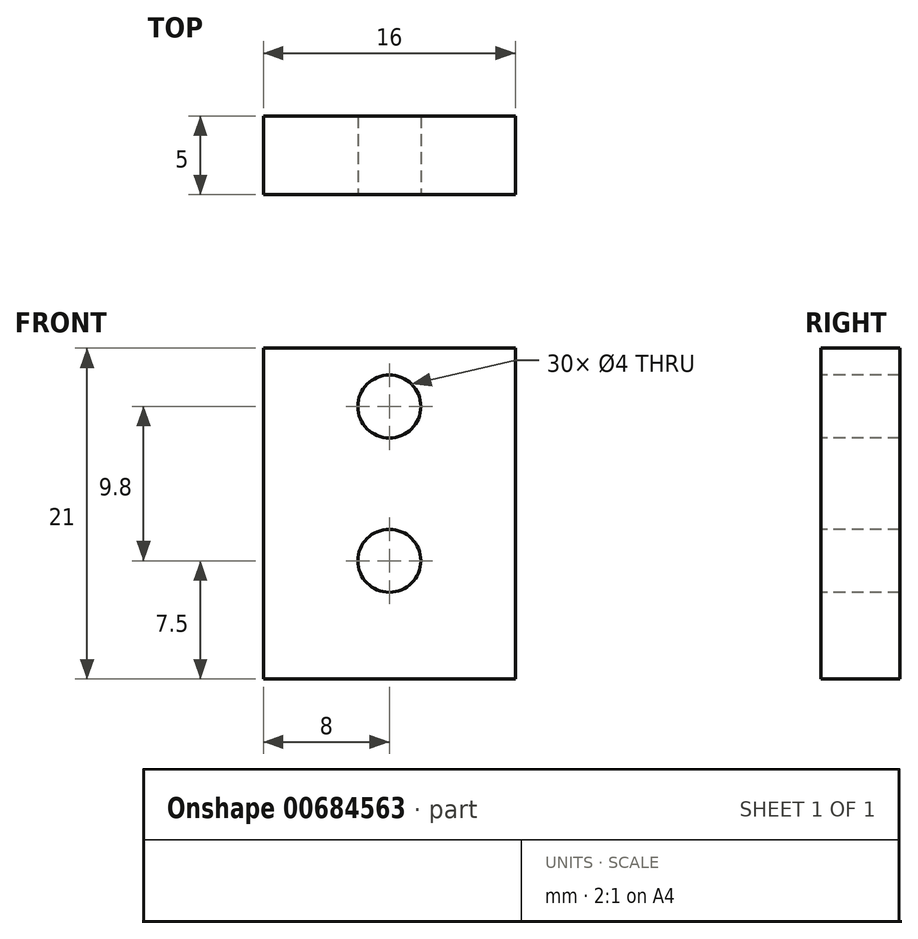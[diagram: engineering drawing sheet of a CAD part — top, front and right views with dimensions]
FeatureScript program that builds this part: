
annotation { "Feature Type Name" : "Feature", "Feature Type Description" : "" }
export const myFeature = defineFeature(function(context is Context, id is Id, definition is map)
    precondition{}
    {
        {
            var Q0;
            Q0=qCreatedBy(makeId("Front.planeOp"),FACE);
            var sketch = newSketch(context, id + "F0", { "sketchPlane" : qUnion([Q0])});
            skLineSegment(sketch, "E0.bottom", {"start": v(0, 0) * mm, "end": v(16, 0) * mm});
            skLineSegment(sketch, "E0.top", {"start": v(0, 21) * mm, "end": v(16, 21) * mm});
            skLineSegment(sketch, "E0.left", {"start": v(0, 0) * mm, "end": v(0, 21) * mm});
            skLineSegment(sketch, "E0.right", {"start": v(16, 0) * mm, "end": v(16, 21) * mm});
            skSolve(sketch);
        }
        {
            var Q0;
            Q0=makeQuery(id+"F0.imprint","IMPRINT",FACE,{"disambiguationData":[TD([[makeQuery(id+"F0.imprint","IMPRINT",EDGE,{"derivedFrom":sQuery(id+"F0.wireOp",EDGE,"E0.bottom")}),1.0]])]});
            extrude(context, id + "F1", {"entities" : qUnion([Q0]), "depth" : 5 * mm});
        }
        {
            var Q0;
            Q0=makeQuery(id+"F1.opExtrude","CAP_FACE",FACE,{"disambiguationData":[OSD([sQuery(id+"F0.wireOp",EDGE,"E0.bottom"),sQuery(id+"F0.wireOp",EDGE,"E0.top"),sQuery(id+"F0.wireOp",EDGE,"E0.left"),sQuery(id+"F0.wireOp",EDGE,"E0.right")])],"isStart":false});
            var sketch = newSketch(context, id + "F2", { "sketchPlane" : qUnion([Q0])});
            skCircle(sketch, "E1", {"center": v(8, 7.5) * mm, "radius": 2 * mm});
            skCircle(sketch, "E2", {"center": v(8, 17.3) * mm, "radius": 2 * mm});
            skSolve(sketch);
        }
        {
            var Q0;
            Q0=makeQuery(id+"F2.imprint","IMPRINT",FACE,{"disambiguationData":[TD([[makeQuery(id+"F2.imprint","IMPRINT",EDGE,{"derivedFrom":sQuery(id+"F2.wireOp",EDGE,"E2")}),1.0]])]});
            var Q1;
            Q1=makeQuery(id+"F2.imprint","IMPRINT",FACE,{"disambiguationData":[TD([[makeQuery(id+"F2.imprint","IMPRINT",EDGE,{"derivedFrom":sQuery(id+"F2.wireOp",EDGE,"E1")}),1.0]])]});
            extrude(context, id + "F3", {"entities" : qUnion([Q0, Q1]), "operationType" : NewBodyOperationType.REMOVE, "endBound" : BoundingType.THROUGH_ALL, "oppositeDirection" : true, "depth" : 25 * mm});
        }
    });
